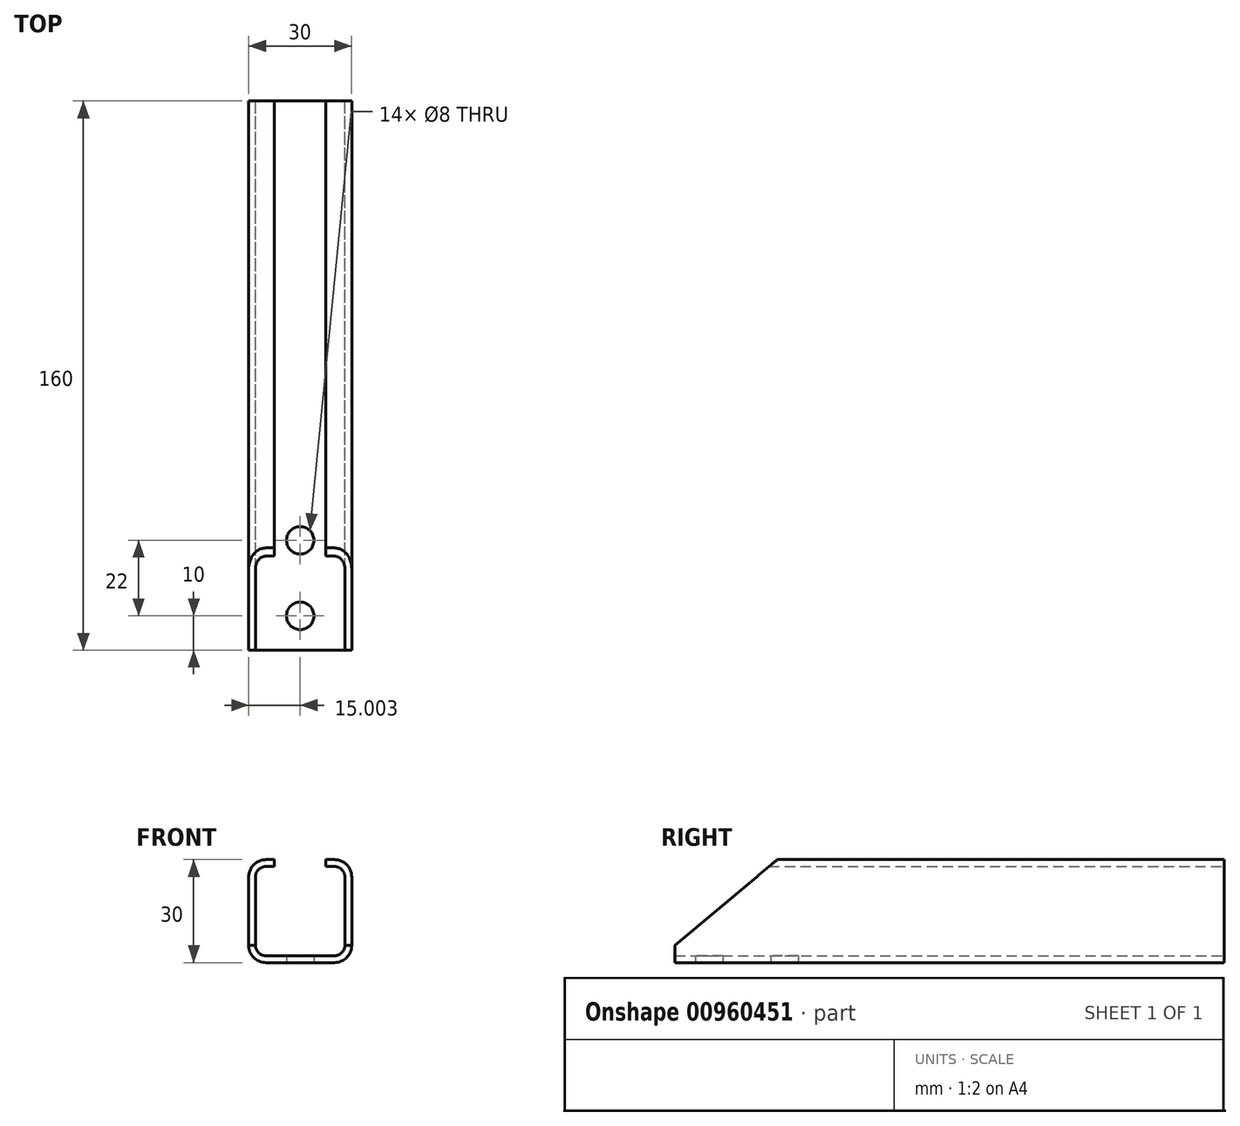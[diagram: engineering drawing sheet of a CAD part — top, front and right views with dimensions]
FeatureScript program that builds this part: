
annotation { "Feature Type Name" : "Feature", "Feature Type Description" : "" }
export const myFeature = defineFeature(function(context is Context, id is Id, definition is map)
    precondition{}
    {
        {
            var Q0;
            Q0=qCreatedBy(makeId("Front.planeOp"),FACE);
            var sketch = newSketch(context, id + "F0", { "sketchPlane" : qUnion([Q0])});
            skLineSegment(sketch, "E0.bottom", {"start": v(-20.95, -2.52) * mm, "end": v(-40.95, -2.52) * mm});
            skLineSegment(sketch, "E0.top", {"start": v(-20.95, -32.52) * mm, "end": v(-40.95, -32.52) * mm});
            skLineSegment(sketch, "E0.left", {"start": v(-15.95, -7.52) * mm, "end": v(-15.95, -27.52) * mm});
            skLineSegment(sketch, "E0.right", {"start": v(-45.95, -7.52) * mm, "end": v(-45.95, -27.52) * mm});
            skPoint(sketch, "E0.middle", {"position": v(-30.95, -17.52) * mm});
            skPoint(sketch, "E1.visualSharp", {"position": v(-45.95, -2.52) * mm});
            skArc(sketch, "E1.filletArc", {"start": v(-40.95, -2.52) * mm, "mid": v(-44.48, -3.98) * mm, "end": v(-45.95, -7.52) * mm});
            skPoint(sketch, "E2.visualSharp", {"position": v(-15.95, -2.52) * mm});
            skArc(sketch, "E2.filletArc", {"start": v(-15.95, -7.52) * mm, "mid": v(-17.41, -3.98) * mm, "end": v(-20.95, -2.52) * mm});
            skPoint(sketch, "E3.visualSharp", {"position": v(-15.95, -32.52) * mm});
            skArc(sketch, "E3.filletArc", {"start": v(-20.95, -32.52) * mm, "mid": v(-17.41, -31.05) * mm, "end": v(-15.95, -27.52) * mm});
            skPoint(sketch, "E4.visualSharp", {"position": v(-45.95, -32.52) * mm});
            skArc(sketch, "E4.filletArc", {"start": v(-45.95, -27.52) * mm, "mid": v(-44.48, -31.05) * mm, "end": v(-40.95, -32.52) * mm});
            skLineSegment(sketch, "E5.0", {"start": v(-43.95, -7.52) * mm, "end": v(-43.95, -27.52) * mm});
            skLineSegment(sketch, "E5.1", {"start": v(-20.95, -4.52) * mm, "end": v(-40.95, -4.52) * mm});
            skLineSegment(sketch, "E5.2", {"start": v(-17.95, -7.52) * mm, "end": v(-17.95, -27.52) * mm});
            skLineSegment(sketch, "E5.3", {"start": v(-20.95, -30.52) * mm, "end": v(-40.95, -30.52) * mm});
            skPoint(sketch, "E6.visualSharp", {"position": v(-43.95, -4.52) * mm});
            skArc(sketch, "E6.filletArc", {"start": v(-40.95, -4.52) * mm, "mid": v(-43.07, -5.4) * mm, "end": v(-43.95, -7.52) * mm});
            skPoint(sketch, "E7.visualSharp", {"position": v(-43.95, -30.52) * mm});
            skArc(sketch, "E7.filletArc", {"start": v(-43.95, -27.52) * mm, "mid": v(-43.07, -29.64) * mm, "end": v(-40.95, -30.52) * mm});
            skPoint(sketch, "E8.visualSharp", {"position": v(-17.95, -30.52) * mm});
            skArc(sketch, "E8.filletArc", {"start": v(-20.95, -30.52) * mm, "mid": v(-18.83, -29.64) * mm, "end": v(-17.95, -27.52) * mm});
            skPoint(sketch, "E9.visualSharp", {"position": v(-17.95, -4.52) * mm});
            skArc(sketch, "E9.filletArc", {"start": v(-17.95, -7.52) * mm, "mid": v(-18.83, -5.4) * mm, "end": v(-20.95, -4.52) * mm});
            skLineSegment(sketch, "E10", {"start": v(-38.45, -4.52) * mm, "end": v(-38.45, -2.52) * mm});
            skLineSegment(sketch, "E11", {"start": v(-30.95, -17.52) * mm, "end": v(-30.95, 7.92) * mm});
            skLineSegment(sketch, "E12.MirrorCS", {"start": v(-23.45, -4.52) * mm, "end": v(-23.45, -2.52) * mm});
            skSolve(sketch);
        }
        {
            var Q0;
            Q0=makeQuery(id+"F0.imprint","IMPRINT",FACE,{"disambiguationData":[TD([[makeQuery(id+"F0.imprint","IMPRINT",EDGE,{"derivedFrom":sQuery(id+"F0.wireOp",EDGE,"E0.top")}),-1.0]])]});
            extrude(context, id + "F1", {"entities" : qUnion([Q0]), "depth" : 160 * mm, "offsetDistance" : 25 * mm});
        }
        {
            var Q0;
            Q0=makeQuery(id+"F1.opExtrude","SWEPT_FACE",FACE,{"disambiguationData":[OSD([sQuery(id+"F0.wireOp",EDGE,"E0.right")])]});
            var sketch = newSketch(context, id + "F2", { "sketchPlane" : qUnion([Q0])});
            skLineSegment(sketch, "E13", {"start": v(160, -27.52) * mm, "end": v(121.25, 5) * mm});
            skLineSegment(sketch, "E14", {"start": v(121.25, 5) * mm, "end": v(160, 5) * mm});
            skLineSegment(sketch, "E15", {"start": v(160, 5) * mm, "end": v(160, -27.52) * mm});
            skSolve(sketch);
        }
        {
            var Q0;
            Q0 = qSketchRegion(id + "F2", true);
            extrude(context, id + "F3", {"entities" : qUnion([Q0]), "operationType" : NewBodyOperationType.REMOVE, "oppositeDirection" : true, "depth" : 32 * mm, "offsetDistance" : 25 * mm});
        }
        {
            var Q0;
            Q0=makeQuery(id+"F1.opExtrude","SWEPT_FACE",FACE,{"disambiguationData":[OSD([sQuery(id+"F0.wireOp",EDGE,"E0.top")])]});
            var sketch = newSketch(context, id + "F4", { "sketchPlane" : qUnion([Q0])});
            skCircle(sketch, "E16", {"center": v(-30.95, 150) * mm, "radius": 4 * mm});
            skPoint(sketch, "E16.centerSnap0", {"position": v(-30.95, 160) * mm});
            skCircle(sketch, "E17", {"center": v(-30.95, 128) * mm, "radius": 4 * mm});
            skSolve(sketch);
        }
        {
            var Q0;
            Q0 = qSketchRegion(id + "F4", true);
            extrude(context, id + "F5", {"entities" : qUnion([Q0]), "operationType" : NewBodyOperationType.REMOVE, "oppositeDirection" : true, "depth" : 25 * mm, "offsetDistance" : 25 * mm});
        }
    });
